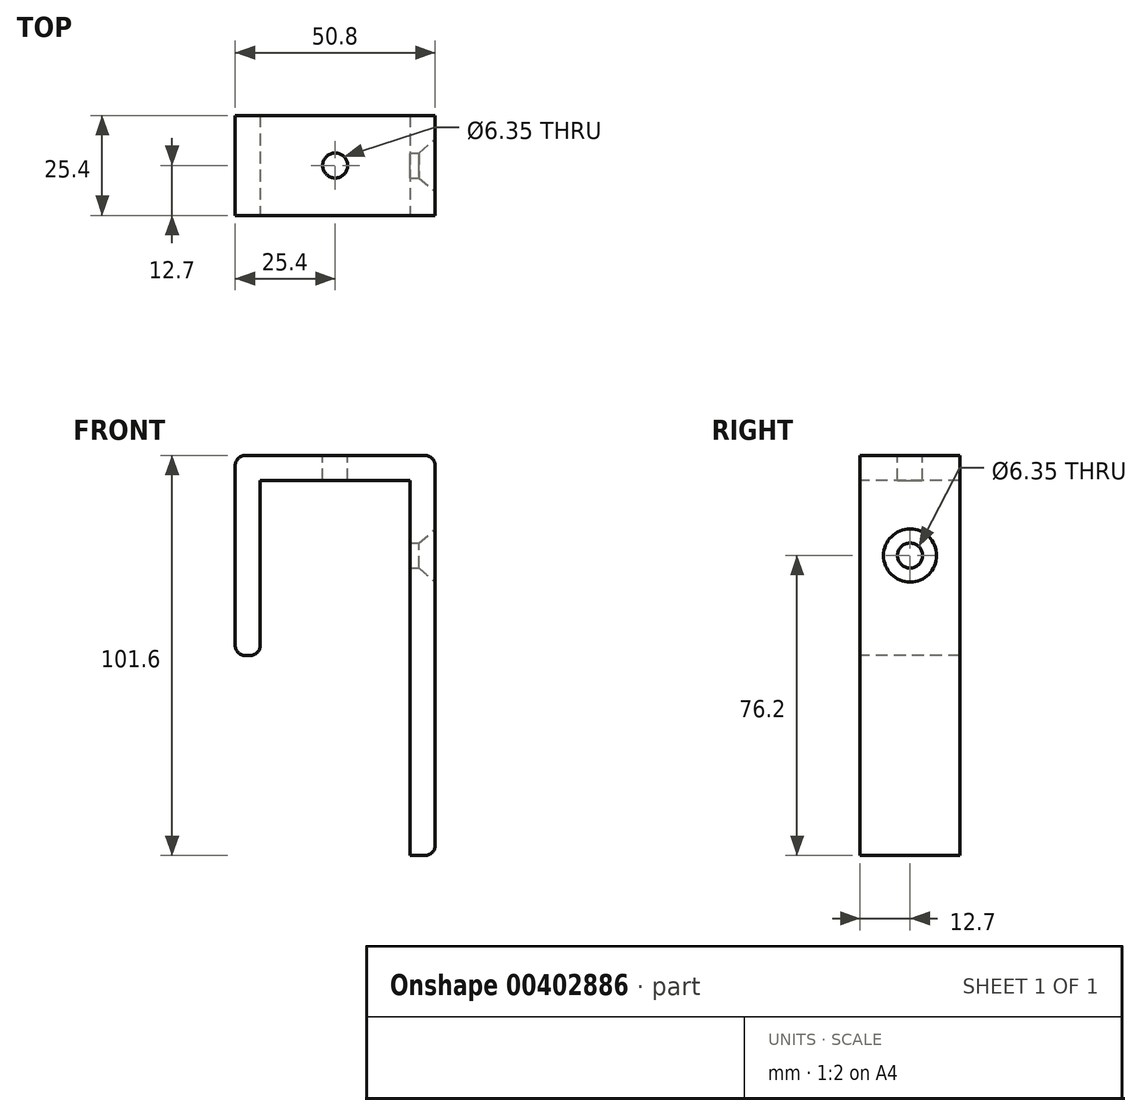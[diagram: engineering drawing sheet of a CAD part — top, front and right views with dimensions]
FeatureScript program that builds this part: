
annotation { "Feature Type Name" : "Feature", "Feature Type Description" : "" }
export const myFeature = defineFeature(function(context is Context, id is Id, definition is map)
    precondition{}
    {
        {
            var Q0;
            Q0=qCreatedBy(makeId("Front.planeOp"),FACE);
            var sketch = newSketch(context, id + "F0", { "sketchPlane" : qUnion([Q0])});
            skLineSegment(sketch, "E0", {"start": v(0, 6.35) * mm, "end": v(50.8, 6.35) * mm});
            skLineSegment(sketch, "E1", {"start": v(50.8, 6.35) * mm, "end": v(50.8, -95.25) * mm});
            skLineSegment(sketch, "E2", {"start": v(50.8, -95.25) * mm, "end": v(44.45, -95.25) * mm});
            skLineSegment(sketch, "E3", {"start": v(44.45, -95.25) * mm, "end": v(44.45, 0) * mm});
            skLineSegment(sketch, "E4", {"start": v(44.45, 0) * mm, "end": v(6.35, 0) * mm});
            skLineSegment(sketch, "E5", {"start": v(6.35, 0) * mm, "end": v(6.35, -44.45) * mm});
            skLineSegment(sketch, "E6", {"start": v(6.35, -44.45) * mm, "end": v(0, -44.45) * mm});
            skLineSegment(sketch, "E7", {"start": v(0, 6.35) * mm, "end": v(0, -44.45) * mm});
            skSolve(sketch);
        }
        {
            var Q0;
            Q0=makeQuery(id+"F0.imprint","IMPRINT",FACE,{"disambiguationData":[TD([[makeQuery(id+"F0.imprint","IMPRINT",EDGE,{"derivedFrom":sQuery(id+"F0.wireOp",EDGE,"E0")}),-1.0]])]});
            extrude(context, id + "F1", {"entities" : qUnion([Q0]), "oppositeDirection" : true, "depth" : 25.4 * mm});
        }
        {
            var Q0;
            Q0=makeQuery(id+"F1.opExtrude","SWEPT_FACE",FACE,{"disambiguationData":[OSD([sQuery(id+"F0.wireOp",EDGE,"E1")])]});
            var sketch = newSketch(context, id + "F2", { "sketchPlane" : qUnion([Q0])});
            skLineSegment(sketch, "E8", {"start": v(12.7, 6.35) * mm, "end": v(12.7, -19.05) * mm, "construction": true});
            skPoint(sketch, "E9", {"position": v(12.7, -19.05) * mm});
            skLineSegment(sketch, "E10", {"start": v(12.7, -19.05) * mm, "end": v(12.7, -63.5) * mm, "construction": true});
            skPoint(sketch, "E11", {"position": v(12.7, -63.5) * mm});
            skSolve(sketch);
        }
        {
            var Q0;
            Q0=makeQuery(id+"F1.opExtrude","SWEPT_FACE",FACE,{"disambiguationData":[OSD([sQuery(id+"F0.wireOp",EDGE,"E0")])]});
            var sketch = newSketch(context, id + "F3", { "sketchPlane" : qUnion([Q0])});
            skLineSegment(sketch, "E12", {"start": v(50.8, 12.7) * mm, "end": v(25.4, 12.7) * mm, "construction": true});
            skPoint(sketch, "E12.endSnap0", {"position": v(50.8, 12.7) * mm});
            skPoint(sketch, "E13", {"position": v(25.4, 12.7) * mm});
            skSolve(sketch);
        }
        {
            var Q0;
            Q0=sQuery(id+"F2.wireOp",VERTEX,"E9");
            var Q1;
            Q1=makeQuery(id+"F1.opExtrude","SWEPT_BODY",BODY,{"disambiguationData":[OSD([sQuery(id+"F0.wireOp",EDGE,"E0"),sQuery(id+"F0.wireOp",EDGE,"E1"),sQuery(id+"F0.wireOp",EDGE,"E2"),sQuery(id+"F0.wireOp",EDGE,"E3"),sQuery(id+"F0.wireOp",EDGE,"E4"),sQuery(id+"F0.wireOp",EDGE,"E5"),sQuery(id+"F0.wireOp",EDGE,"E6"),sQuery(id+"F0.wireOp",EDGE,"E7")])]});
            hole(context, id + "F4", {"style" : HoleStyle.C_SINK, "endStyle" : HoleEndStyle.BLIND, "holeDiameter" : 6.35 * mm, "cSinkDiameter" : 13.5 * mm, "cSinkAngle" : 82 * degree, "holeDepth" : 12.7 * mm, "isTappedThrough" : true, "tappedDepth" : 12.7 * mm, "tapClearance" : 3, "startFromSketch" : true, "locations" : qUnion([Q0]), "scope" : qUnion([Q1])});
        }
        {
            var Q0;
            Q0=sQuery(id+"F3.wireOp",VERTEX,"E13");
            var Q1;
            Q1=makeQuery(id+"F1.opExtrude","SWEPT_BODY",BODY,{"disambiguationData":[OSD([sQuery(id+"F0.wireOp",EDGE,"E0"),sQuery(id+"F0.wireOp",EDGE,"E1"),sQuery(id+"F0.wireOp",EDGE,"E2"),sQuery(id+"F0.wireOp",EDGE,"E3"),sQuery(id+"F0.wireOp",EDGE,"E4"),sQuery(id+"F0.wireOp",EDGE,"E5"),sQuery(id+"F0.wireOp",EDGE,"E6"),sQuery(id+"F0.wireOp",EDGE,"E7")])]});
            hole(context, id + "F5", {"style" : HoleStyle.SIMPLE, "endStyle" : HoleEndStyle.BLIND, "holeDiameter" : 6.35 * mm, "holeDepth" : 12.7 * mm, "isTappedThrough" : true, "tappedDepth" : 12.7 * mm, "tapClearance" : 3, "startFromSketch" : true, "locations" : qUnion([Q0]), "scope" : qUnion([Q1])});
        }
        {
            var Q0;
            Q0=makeQuery(id+"F1.opExtrude","SWEPT_EDGE",EDGE,{"disambiguationData":[OSD([sQuery(id+"F0.wireOp",EDGE,"E0"),sQuery(id+"F0.wireOp",EDGE,"E7")])]});
            var Q1;
            Q1=makeQuery(id+"F1.opExtrude","SWEPT_EDGE",EDGE,{"disambiguationData":[OSD([sQuery(id+"F0.wireOp",EDGE,"E0"),sQuery(id+"F0.wireOp",EDGE,"E1")])]});
            fillet(context, id + "F6", {"entities" : qUnion([Q0, Q1]), "radius" : 2.54 * mm, "tangentPropagation" : true, "allowEdgeOverflow" : false});
        }
        {
            var Q0;
            Q0=makeQuery(id+"F1.opExtrude","SWEPT_EDGE",EDGE,{"disambiguationData":[OSD([sQuery(id+"F0.wireOp",EDGE,"E1"),sQuery(id+"F0.wireOp",EDGE,"E2")])]});
            var Q1;
            Q1=makeQuery(id+"F1.opExtrude","SWEPT_EDGE",EDGE,{"disambiguationData":[OSD([sQuery(id+"F0.wireOp",EDGE,"E5"),sQuery(id+"F0.wireOp",EDGE,"E6")])]});
            var Q2;
            Q2=makeQuery(id+"F1.opExtrude","SWEPT_EDGE",EDGE,{"disambiguationData":[OSD([sQuery(id+"F0.wireOp",EDGE,"E6"),sQuery(id+"F0.wireOp",EDGE,"E7")])]});
            fillet(context, id + "F7", {"entities" : qUnion([Q0, Q1, Q2]), "radius" : 2.54 * mm, "tangentPropagation" : true, "allowEdgeOverflow" : false});
        }
    });
